# Revit family: ARON_RECESSED_LUMINAIRE
name_source: partatom
category: Lighting Fixtures
revit_build: Autodesk Revit 2016 (Build: 20151209_0715(x64)
units: mm (PartAtom-declared; Revit-internal decimal feet)

## family parameters
Cut with Voids When Loaded = No
Host = Face
Light Source = Yes
OmniClass Number = 23.80.70.11.17
OmniClass Title = Specialized Lighting by Location or Use
Part Type = Normal
Room Calculation Point = No
Round Connector Dimension = Use Diameter
Shared = No

## types (18) — shared parameters
120 Volts = Yes
Apparent Load = 32 VA
Color Filter = 16777215
Default Elevation = 0' - 0"
Description = T-Bar DUO Luminaire
Dimming Lamp Color Temperature Shift = <None>
Electrical Casing Material = Stainless Steel
Emit Shape Visible in Rendering = Yes
Emit from Rectangle Width = 0' - 6"
End Cap Material = White Plastic
Housing Material = White Painted Aluminum
Illuminated Surface Material = Frosted Acrylic Lens
Lamp Quantity = 2
Load Classification = Lighting
Manufacturer = ARON
Mounting = Recessed
Tilt Angle = -90.00°
URL = http://www.aronlighting.com
Void Width = 0' - 6"

## per-type parameters (varying)
| type | Emit from Rectangle Length | Lumens Per Lamp | Luminaire Length | Model | Photometric Web File | Series | Total Lumens | Void Length | Voltage |
| TBAR-2FT-3000K-UNV-2000-B2-80-DM | 2' - 0 15/16" | 1000 lm | 2' - 0" | TBAR-2FT-300K-UNV-2000-B2-80-DM | TBAR-2FT-3000K-UNV-2000-B2-80-DM.ies | TBAR | 2000 lm | 2' - 0 15/16" | 120 V |
| TBAR-2FT-3000K-UNV-2500-B2-80-DM | 2' - 0 15/16" | 1250 lm | 2' - 0" | TBAR-2FT-3000K-UNV-2500-B2-80-DM | TBAR-2FT-3000K-UNV-2500-B2-80-DM.ies | TBAR | 2500 lm | 2' - 0 15/16" | 120 V |
| TBAR-2FT-3000K-UNV-3000-B2-80-DM | 2' - 0 15/16" | 1500 lm | 2' - 0" | TBAR-2FT-3000K-UNV-3000-B2-80-DM | TBAR-2FT-3000K-UNV-3000-B2-80-DM.ies |  | 3000 lm | 2' - 0 15/16" | 120 V |
| TBAR-2FT-3500K-UNV-2000-B2-80-DM | 2' - 0 15/16" | 1000 lm | 2' - 0" | TBAR-2FT-3500K-UNV-2000-B2-80-DM | TBAR-2FT-3500K-UNV-2000-B2-80-DM.ies | TBAR | 2000 lm | 2' - 0 15/16" | 120 V |
| TBAR-2FT-3500K-UNV-2500-B2-80-DM | 2' - 0 15/16" | 1250 lm | 2' - 0" | TBAR-2FT-3500K-UNV-2500-B2-80-DM | TBAR-2FT-3500K-UNV-2500-B2-80-DM.ies | TBAR | 2500 lm | 2' - 0 15/16" | 120 V |
| TBAR-2FT-3500K-UNV-3000-B2-80-DM | 2' - 0 15/16" | 1500 lm | 2' - 0" | TBAR-2FT-3500-UNV-3000-B2-80-DM | TBAR-2FT-3500K-UNV-3000-B2-80-DM.ies | TBAR | 3000 lm | 2' - 0 15/16" | 120 V |
| TBAR-2FT-4000K-UNV-2000-B2-80-DM | 2' - 0 15/16" | 1000 lm | 2' - 0" | TBAR-2FT-4000K-UNV-2000-B2-80-DM | TBAR-2FT-4000K-UNV-2000-B2-80-DM.ies | TBAR | 2000 lm | 2' - 0 15/16" | 120 V |
| TBAR-2FT-4000K-UNV-2500-B2-80-DM | 2' - 0 15/16" | 1250 lm | 2' - 0" | TBAR-2FT-4000K-UNV-2500-B2-80-DM | TBAR-2FT-4000K-UNV-2500-B2-80-DM.ies | TBAR | 2500 lm | 2' - 0 15/16" | 120 V |
| TBAR-2FT-4000K-UNV-3000-B2-80-DM | 2' - 0 15/16" | 1500 lm | 2' - 0" | TBAR-2FT-4000K-UNV-3000-B2-80-DM | TBAR-2FT-4000K-UNV-3000-B2-80-DM.ies | TBAR | 3000 lm | 2' - 0 15/16" | 120 V |
| TBAR-4FT-3000K-UNV-4000-B2-80-DM | 4' - 0 15/16" | 2000 lm | 4' - 0" | TBAR-4FT-3000K-UNV-4000-B2-80-DM | TBAR-4FT-3000K-UNV-4000-B2-80-DM.ies | TBAR | 4000 lm | 4' - 0 15/16" | 277 V |
| TBAR-4FT-3000K-UNV-5000-B2-80-DM | 4' - 0 15/16" | 2500 lm | 4' - 0" | TBAR-4FT-3000K-UNV-5000-B2-80-DM | TBAR-4FT-3000K-UNV-5000-B2-80-DM.ies | TBAR | 5000 lm | 4' - 0 15/16" | 277 V |
| TBAR-4FT-3000K-UNV-6000-B2-80-DM | 4' - 0 15/16" | 3000 lm | 4' - 0" | TBAR-4FT-3000K-UNV-6000-B2-80-DM | TBAR-4FT-3000K-UNV-6000-B2-80-DM.ies | TBAR | 6000 lm | 4' - 0 15/16" | 277 V |
| TBAR-4FT-3500K-UNV-4000-B2-80-DM | 4' - 0 15/16" | 2000 lm | 4' - 0" | TBAR-4FT-3500K-UNV-4000-B2-80-DM | TBAR-4FT-3500K-UNV-4000-B2-80-DM.ies | TBAR | 4000 lm | 4' - 0 15/16" | 277 V |
| TBAR-4FT-3500K-UNV-5000-B2-80-DM | 4' - 0 15/16" | 2500 lm | 4' - 0" | TBAR-4FT-3500K-UNV-5000-B2-80-DM | TBAR-4FT-3500K-UNV-5000-B2-80-DM.ies | TBAR | 5000 lm | 4' - 0 15/16" | 277 V |
| TBAR-4FT-3500K-UNV-6000-B2-80-DM | 4' - 0 15/16" | 3000 lm | 4' - 0" | TBAR-4FT-3500K-UNV-6000-B2-80-DM | TBAR-4FT-3500K-UNV-6000-B2-80-DM.ies | TBAR | 6000 lm | 4' - 0 15/16" | 277 V |
| TBAR-4FT-4000K-UNV-4000-B2-80-DM | 4' - 0 15/16" | 2000 lm | 4' - 0" | TBAR-4FT-4000K-UNV-4000-B2-80-DM | TBAR-4FT-4000K-UNV-4000-B2-80-DM.ies | TBAR | 4000 lm | 4' - 0 15/16" | 277 V |
| TBAR-4FT-4000K-UNV-5000-B2-80-DM | 4' - 0 15/16" | 2500 lm | 4' - 0" | TBAR-4FT-4000K-UNV-5000-B2-80-DM | TBAR-4FT-4000K-UNV-5000-B2-80-DM.ies | TBAR | 5000 lm | 4' - 0 15/16" | 277 V |
| TBAR-4FT-4000K-UNV-6000-B2-80-DM | 4' - 0 15/16" | 3000 lm | 4' - 0" | TBAR-4FT-4000K-UNV-6000-B2-80-DM | TBAR-4FT-4000K-UNV-6000-B2-80-DM.ies | TBAR | 6000 lm | 4' - 0 15/16" | 277 V |

## geometry (parser evidence)
native form markers: Blend x8, Sweep x28
no freeform markers — native parametric forms only
